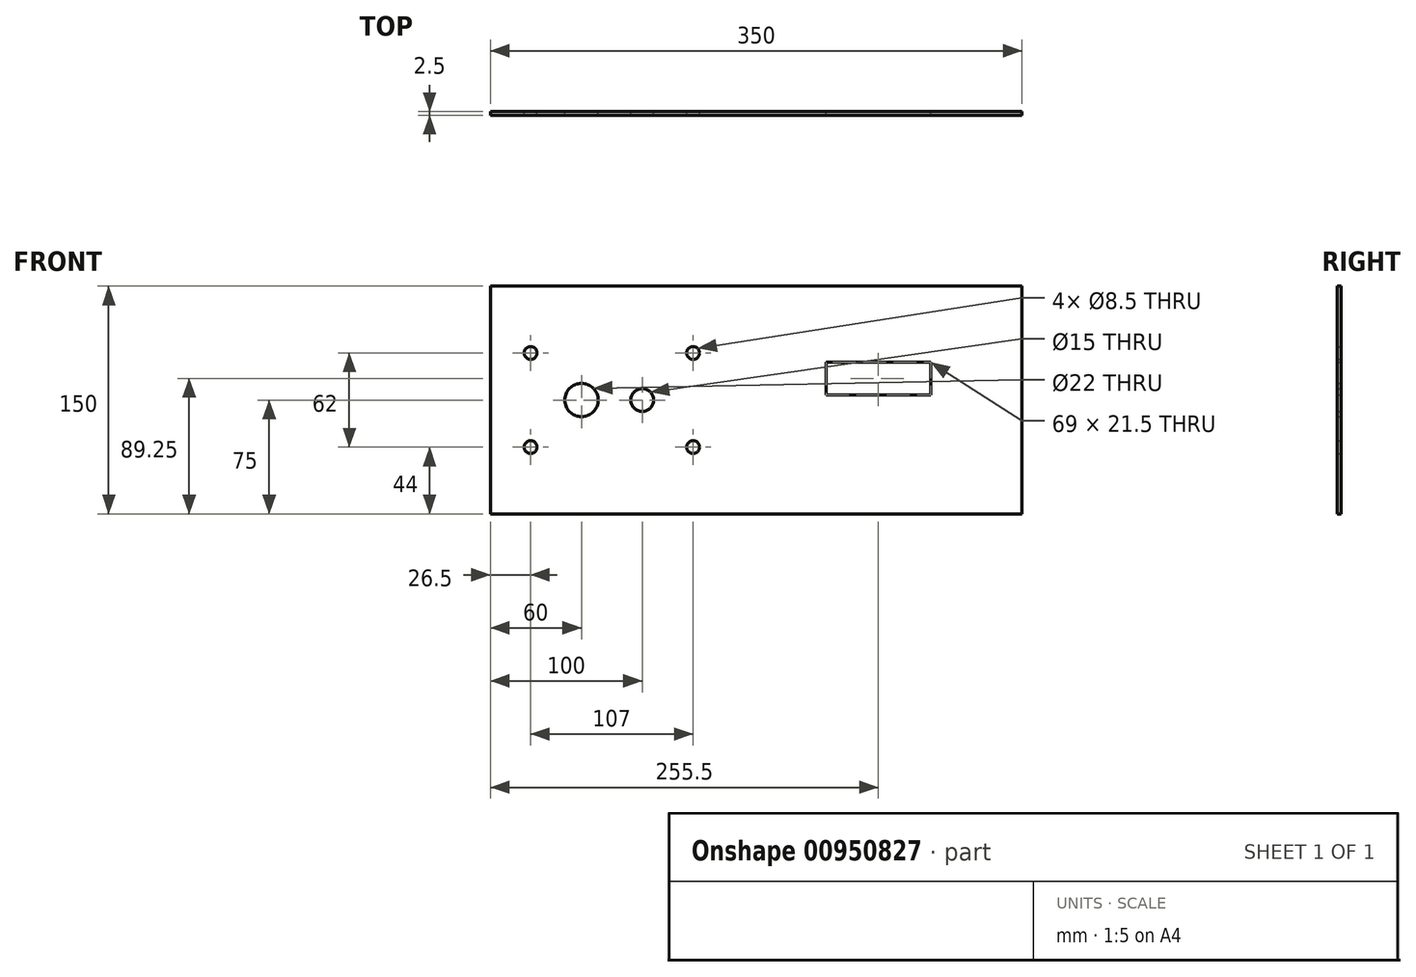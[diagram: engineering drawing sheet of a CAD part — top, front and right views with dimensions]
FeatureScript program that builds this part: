
annotation { "Feature Type Name" : "Feature", "Feature Type Description" : "" }
export const myFeature = defineFeature(function(context is Context, id is Id, definition is map)
    precondition{}
    {
        {
            var Q0;
            Q0=qCreatedBy(makeId("Front.planeOp"),FACE);
            var sketch = newSketch(context, id + "F0", { "sketchPlane" : qUnion([Q0])});
            skLineSegment(sketch, "E0.bottom", {"start": v(175, 75) * mm, "end": v(-175, 75) * mm});
            skLineSegment(sketch, "E0.top", {"start": v(175, -75) * mm, "end": v(-175, -75) * mm});
            skLineSegment(sketch, "E0.left", {"start": v(175, 75) * mm, "end": v(175, -75) * mm});
            skLineSegment(sketch, "E0.right", {"start": v(-175, 75) * mm, "end": v(-175, -75) * mm});
            skPoint(sketch, "E0.middle", {"position": v(0, 0) * mm});
            skCircle(sketch, "E1", {"center": v(-115, 0) * mm, "radius": 11 * mm});
            skCircle(sketch, "E2", {"center": v(-75, 0) * mm, "radius": 7.5 * mm});
            skCircle(sketch, "E3", {"center": v(-148.5, 31) * mm, "radius": 4.25 * mm});
            skCircle(sketch, "E4", {"center": v(-148.5, -31) * mm, "radius": 4.25 * mm});
            skCircle(sketch, "E5", {"center": v(-41.5, -31) * mm, "radius": 4.25 * mm});
            skCircle(sketch, "E6", {"center": v(-41.5, 31) * mm, "radius": 4.25 * mm});
            skLineSegment(sketch, "E7.bottom", {"start": v(46, 25) * mm, "end": v(115, 25) * mm});
            skLineSegment(sketch, "E7.top", {"start": v(46, 3.5) * mm, "end": v(115, 3.5) * mm});
            skLineSegment(sketch, "E7.left", {"start": v(46, 25) * mm, "end": v(46, 3.5) * mm});
            skLineSegment(sketch, "E7.right", {"start": v(115, 25) * mm, "end": v(115, 3.5) * mm});
            skSolve(sketch);
        }
        {
            var Q0;
            Q0=qSketchRegion(id+"F0",true);
            extrude(context, id + "F1", {"entities" : qUnion([Q0]), "depth" : 2.5 * mm, "offsetDistance" : 25 * mm});
        }
    });
